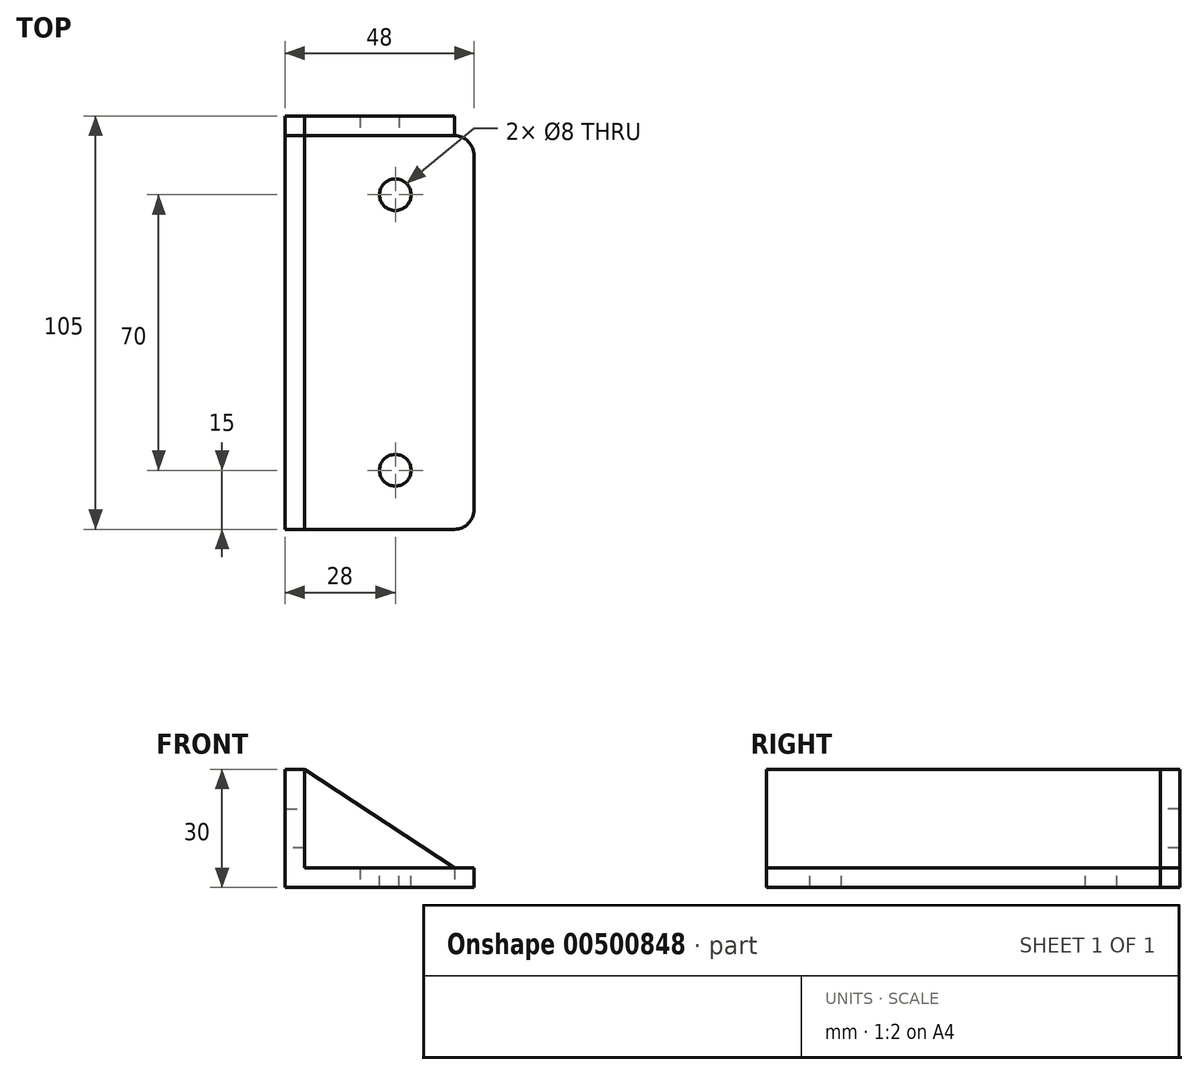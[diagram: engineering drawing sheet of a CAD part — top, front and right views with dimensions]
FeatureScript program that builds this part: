
annotation { "Feature Type Name" : "Feature", "Feature Type Description" : "" }
export const myFeature = defineFeature(function(context is Context, id is Id, definition is map)
    precondition{}
    {
        {
            var Q0;
            Q0=qCreatedBy(makeId("Front.planeOp"),FACE);
            var sketch = newSketch(context, id + "F0", { "sketchPlane" : qUnion([Q0])});
            skLineSegment(sketch, "E0", {"start": v(0, 0) * mm, "end": v(0, 30) * mm});
            skLineSegment(sketch, "E1", {"start": v(0, 30) * mm, "end": v(5, 30) * mm});
            skLineSegment(sketch, "E2", {"start": v(5, 30) * mm, "end": v(5, 5) * mm});
            skLineSegment(sketch, "E3", {"start": v(5, 5) * mm, "end": v(48, 5) * mm});
            skLineSegment(sketch, "E4", {"start": v(48, 5) * mm, "end": v(48, 0) * mm});
            skLineSegment(sketch, "E5", {"start": v(48, 0) * mm, "end": v(0, 0) * mm});
            skSolve(sketch);
        }
        {
            var Q0;
            Q0 = qSketchRegion(id + "F0", true);
            extrude(context, id + "F1", {"entities" : qUnion([Q0]), "depth" : 100 * mm, "offsetDistance" : 25 * mm});
        }
        {
            var Q0;
            Q0=makeQuery(id+"F1.opExtrude","SWEPT_FACE",FACE,{"disambiguationData":[OSD([sQuery(id+"F0.wireOp",EDGE,"E3")])]});
            var sketch = newSketch(context, id + "F2", { "sketchPlane" : qUnion([Q0])});
            skPoint(sketch, "E6", {"position": v(28, -85) * mm});
            skPoint(sketch, "E7", {"position": v(28, -15) * mm});
            skCircle(sketch, "E8", {"center": v(28, -85) * mm, "radius": 4 * mm});
            skCircle(sketch, "E9", {"center": v(28, -15) * mm, "radius": 4 * mm});
            skSolve(sketch);
        }
        {
            var Q0;
            Q0 = qSketchRegion(id + "F2", true);
            extrude(context, id + "F3", {"entities" : qUnion([Q0]), "operationType" : NewBodyOperationType.REMOVE, "oppositeDirection" : true, "depth" : 25 * mm, "offsetDistance" : 25 * mm});
        }
        {
            var Q0;
            Q0=makeQuery(id+"F1.opExtrude","CAP_EDGE",EDGE,{"disambiguationData":[OSD([sQuery(id+"F0.wireOp",EDGE,"E4")])],"isStart":false});
            var Q1;
            Q1=makeQuery(id+"F1.opExtrude","CAP_EDGE",EDGE,{"disambiguationData":[OSD([sQuery(id+"F0.wireOp",EDGE,"E4")])],"isStart":true});
            fillet(context, id + "F4", {"entities" : qUnion([Q0, Q1]), "radius" : 5 * mm, "tangentPropagation" : true, "allowEdgeOverflow" : false});
        }
        {
            var Q0;
            Q0=makeQuery(id+"F1.opExtrude","CAP_FACE",FACE,{"disambiguationData":[OSD([sQuery(id+"F0.wireOp",EDGE,"E0"),sQuery(id+"F0.wireOp",EDGE,"E1"),sQuery(id+"F0.wireOp",EDGE,"E2"),sQuery(id+"F0.wireOp",EDGE,"E3"),sQuery(id+"F0.wireOp",EDGE,"E4"),sQuery(id+"F0.wireOp",EDGE,"E5")])],"isStart":true});
            var sketch = newSketch(context, id + "F5", { "sketchPlane" : qUnion([Q0])});
            skLineSegment(sketch, "E10", {"start": v(0, 15) * mm, "end": v(0, 20) * mm});
            skLineSegment(sketch, "E11", {"start": v(0, 20) * mm, "end": v(-5, 20) * mm});
            skLineSegment(sketch, "E12", {"start": v(-5, 20) * mm, "end": v(-5, 10) * mm});
            skLineSegment(sketch, "E13", {"start": v(-5, 10) * mm, "end": v(0, 10) * mm});
            skLineSegment(sketch, "E14", {"start": v(0, 10) * mm, "end": v(0, 15) * mm});
            skLineSegment(sketch, "E15", {"start": v(-24, 5) * mm, "end": v(-19, 5) * mm});
            skLineSegment(sketch, "E16", {"start": v(-19, 5) * mm, "end": v(-19, 0) * mm});
            skLineSegment(sketch, "E17", {"start": v(-19, 0) * mm, "end": v(-29, 0) * mm});
            skLineSegment(sketch, "E18", {"start": v(-29, 0) * mm, "end": v(-29, 5) * mm});
            skLineSegment(sketch, "E19", {"start": v(-29, 5) * mm, "end": v(-24, 5) * mm});
            skSolve(sketch);
        }
        {
            var Q0;
            Q0 = qSketchRegion(id + "F5", true);
            extrude(context, id + "F6", {"entities" : qUnion([Q0]), "operationType" : NewBodyOperationType.ADD, "depth" : 5 * mm, "offsetDistance" : 25 * mm});
        }
        {
            var Q0;
            Q0=qCreatedBy(makeId("Front.planeOp"),FACE);
            cPlane(context, id + "F7", {"entities" : qUnion([Q0]), "cplaneType" : CPlaneType.OFFSET, "offset" : 50 * mm, "width" : 150 * mm, "height" : 150 * mm});
        }
        {
            var Q0;
            {var subQ0=sQuery(id+"F0.wireOp",EDGE,"E2");var subQ1=sQuery(id+"F0.wireOp",EDGE,"E1");var subQ2=sQuery(id+"F0.wireOp",EDGE,"E0");Q0=makeQuery(id+"F6.boolean.opBoolean","SPLIT",FACE,{"disambiguationData":[TD([makeQuery(id+"F1.opExtrude","SWEPT_FACE",FACE,{"disambiguationData":[OSD([subQ1])]})])],"derivedFrom":makeQuery(id+"F1.opExtrude","CAP_FACE",FACE,{"disambiguationData":[OSD([subQ2,subQ1,subQ0,sQuery(id+"F0.wireOp",EDGE,"E3"),sQuery(id+"F0.wireOp",EDGE,"E4"),sQuery(id+"F0.wireOp",EDGE,"E5")])],"isStart":true})});}
            var sketch = newSketch(context, id + "F8", { "sketchPlane" : qUnion([Q0])});
            skLineSegment(sketch, "E20.0", {"start": v(0, 30) * mm, "end": v(-5, 30) * mm});
            skLineSegment(sketch, "E21.0", {"start": v(0, 20) * mm, "end": v(0, 30) * mm});
            skLineSegment(sketch, "E22.0", {"start": v(-5, 30) * mm, "end": v(-5, 20) * mm});
            skLineSegment(sketch, "E23.0", {"start": v(0, 20) * mm, "end": v(-5, 20) * mm});
            skLineSegment(sketch, "E24.0", {"start": v(0, 0) * mm, "end": v(0, 10) * mm});
            skLineSegment(sketch, "E25.0", {"start": v(-19, 0) * mm, "end": v(0, 0) * mm});
            skLineSegment(sketch, "E26.0", {"start": v(-5, 5) * mm, "end": v(-19, 5) * mm});
            skLineSegment(sketch, "E27.0", {"start": v(-5, 10) * mm, "end": v(-5, 5) * mm});
            skLineSegment(sketch, "E28.0", {"start": v(-5, 10) * mm, "end": v(0, 10) * mm});
            skLineSegment(sketch, "E29.0", {"start": v(-19, 5) * mm, "end": v(-19, 0) * mm});
            skLineSegment(sketch, "E30.0", {"start": v(-29, 5) * mm, "end": v(-43, 5) * mm});
            skLineSegment(sketch, "E31.0", {"start": v(-43, 0) * mm, "end": v(-29, 0) * mm});
            skLineSegment(sketch, "E32.0", {"start": v(-43, 5) * mm, "end": v(-43, 0) * mm});
            skLineSegment(sketch, "E33", {"start": v(-5, 30) * mm, "end": v(-43, 5) * mm});
            skLineSegment(sketch, "E34.0", {"start": v(-29, 0) * mm, "end": v(-29, 5) * mm});
            skLineSegment(sketch, "E35", {"start": v(-5, 20) * mm, "end": v(-5, 10) * mm});
            skLineSegment(sketch, "E36", {"start": v(-19, 5) * mm, "end": v(-29, 5) * mm});
            skSolve(sketch);
        }
        {
            var Q0;
            Q0=makeQuery(id+"F8.imprint","IMPRINT",FACE,{"disambiguationData":[TD([[makeQuery(id+"F8.imprint","IMPRINT",EDGE,{"derivedFrom":sQuery(id+"F8.wireOp",EDGE,"E22.0")}),-1.0]])]});
            var Q1;
            Q1=makeQuery(id+"F8.imprint","IMPRINT",FACE,{"disambiguationData":[TD([[makeQuery(id+"F8.imprint","IMPRINT",EDGE,{"derivedFrom":sQuery(id+"F8.wireOp",EDGE,"E20.0")}),1.0]])]});
            var Q2;
            Q2=makeQuery(id+"F8.imprint","IMPRINT",FACE,{"disambiguationData":[TD([[makeQuery(id+"F8.imprint","IMPRINT",EDGE,{"derivedFrom":sQuery(id+"F8.wireOp",EDGE,"E24.0")}),1.0]])]});
            var Q3;
            Q3=makeQuery(id+"F8.imprint","IMPRINT",FACE,{"disambiguationData":[TD([[makeQuery(id+"F8.imprint","IMPRINT",EDGE,{"derivedFrom":sQuery(id+"F8.wireOp",EDGE,"E30.0")}),1.0]])]});
            extrude(context, id + "F9", {"entities" : qUnion([Q0, Q1, Q2, Q3]), "depth" : 5 * mm, "offsetDistance" : 25 * mm});
        }
    });
